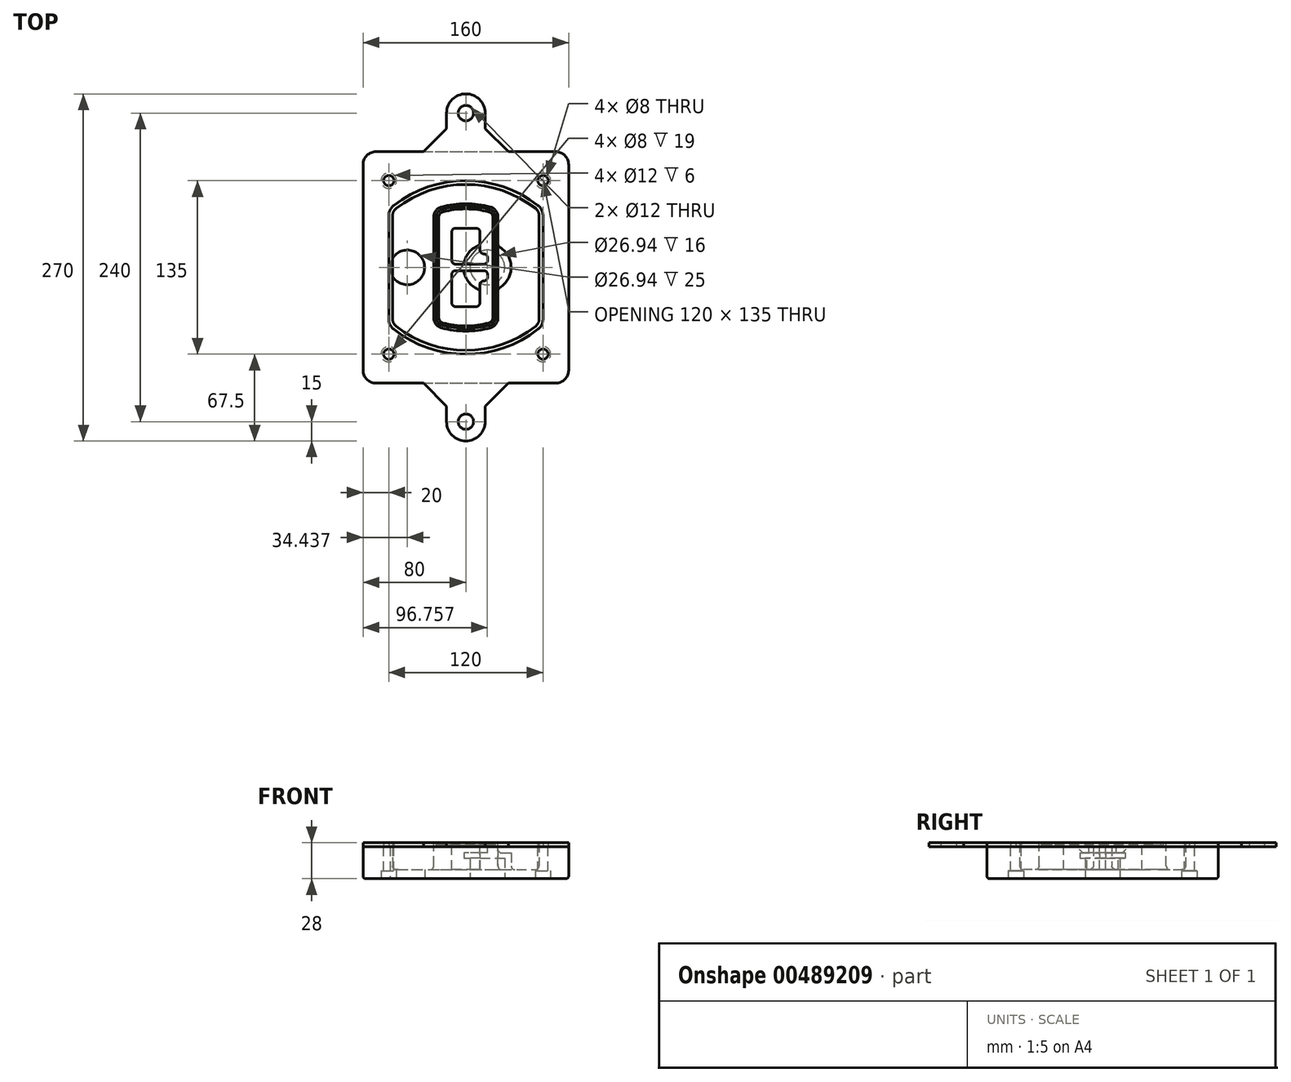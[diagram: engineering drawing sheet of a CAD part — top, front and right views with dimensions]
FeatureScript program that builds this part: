
annotation { "Feature Type Name" : "Feature", "Feature Type Description" : "" }
export const myFeature = defineFeature(function(context is Context, id is Id, definition is map)
    precondition{}
    {
        {
            var Q0;
            Q0=qCreatedBy(makeId("Top.planeOp"),FACE);
            var sketch = newSketch(context, id + "F0", { "sketchPlane" : qUnion([Q0])});
            skPoint(sketch, "E0.rect.middle", {"position": v(0, 0) * mm});
            skLineSegment(sketch, "E1.bottom", {"start": v(-70, -90) * mm, "end": v(70, -90) * mm});
            skLineSegment(sketch, "E1.top", {"start": v(-70, 90) * mm, "end": v(70, 90) * mm});
            skLineSegment(sketch, "E1.left", {"start": v(-80, -80) * mm, "end": v(-80, 80) * mm});
            skLineSegment(sketch, "E1.right", {"start": v(80, -80) * mm, "end": v(80, 80) * mm});
            skLineSegment(sketch, "E2", {"start": v(-80, 90) * mm, "end": v(80, -90) * mm, "construction": true});
            skLineSegment(sketch, "E3", {"start": v(80, 90) * mm, "end": v(-80, -90) * mm, "construction": true});
            skCircle(sketch, "E4", {"center": v(-60, 67.5) * mm, "radius": 4 * mm});
            skCircle(sketch, "E5", {"center": v(60, 67.5) * mm, "radius": 4 * mm});
            skCircle(sketch, "E6", {"center": v(60, -67.5) * mm, "radius": 4 * mm});
            skCircle(sketch, "E7", {"center": v(-60, -67.5) * mm, "radius": 4 * mm});
            skLineSegment(sketch, "E8", {"start": v(-60, 67.5) * mm, "end": v(60, 67.5) * mm, "construction": true});
            skLineSegment(sketch, "E9", {"start": v(60, 67.5) * mm, "end": v(60, -67.5) * mm, "construction": true});
            skLineSegment(sketch, "E10", {"start": v(60, -67.5) * mm, "end": v(-60, -67.5) * mm, "construction": true});
            skLineSegment(sketch, "E11", {"start": v(-60, -67.5) * mm, "end": v(-60, 67.5) * mm, "construction": true});
            skLineSegment(sketch, "E12", {"start": v(-60, 40.3) * mm, "end": v(-60, -40.3) * mm});
            skLineSegment(sketch, "E13", {"start": v(60, 40.3) * mm, "end": v(60, -40.3) * mm});
            skArc(sketch, "E14", {"start": v(56.15, 48.18) * mm, "mid": v(0, 67.5) * mm, "end": v(-56.15, 48.18) * mm});
            skArc(sketch, "E15", {"start": v(-56.15, -48.18) * mm, "mid": v(0, -67.5) * mm, "end": v(56.15, -48.18) * mm});
            skLineSegment(sketch, "E16", {"start": v(-60, 0) * mm, "end": v(60, 0) * mm, "construction": true});
            skPoint(sketch, "E17.visualSharp", {"position": v(-60, -45) * mm});
            skArc(sketch, "E17.filletArc", {"start": v(-60, -40.3) * mm, "mid": v(-58.99, -44.68) * mm, "end": v(-56.15, -48.18) * mm});
            skPoint(sketch, "E18.visualSharp", {"position": v(-60, 45) * mm});
            skArc(sketch, "E18.filletArc", {"start": v(-56.15, 48.18) * mm, "mid": v(-58.99, 44.68) * mm, "end": v(-60, 40.3) * mm});
            skPoint(sketch, "E19.visualSharp", {"position": v(60, 45) * mm});
            skArc(sketch, "E19.filletArc", {"start": v(60, 40.3) * mm, "mid": v(58.99, 44.68) * mm, "end": v(56.15, 48.18) * mm});
            skPoint(sketch, "E20.visualSharp", {"position": v(60, -45) * mm});
            skArc(sketch, "E20.filletArc", {"start": v(56.15, -48.18) * mm, "mid": v(58.99, -44.68) * mm, "end": v(60, -40.3) * mm});
            skPoint(sketch, "E21.visualSharp", {"position": v(-80, 90) * mm});
            skArc(sketch, "E21.filletArc", {"start": v(-70, 90) * mm, "mid": v(-77.07, 87.07) * mm, "end": v(-80, 80) * mm});
            skPoint(sketch, "E22.visualSharp", {"position": v(80, 90) * mm});
            skArc(sketch, "E22.filletArc", {"start": v(80, 80) * mm, "mid": v(77.07, 87.07) * mm, "end": v(70, 90) * mm});
            skPoint(sketch, "E23.visualSharp", {"position": v(80, -90) * mm});
            skArc(sketch, "E23.filletArc", {"start": v(70, -90) * mm, "mid": v(77.07, -87.07) * mm, "end": v(80, -80) * mm});
            skPoint(sketch, "E24.visualSharp", {"position": v(-80, -90) * mm});
            skArc(sketch, "E24.filletArc", {"start": v(-80, -80) * mm, "mid": v(-77.07, -87.07) * mm, "end": v(-70, -90) * mm});
            skArc(sketch, "E25.0", {"start": v(57, 40.3) * mm, "mid": v(56.3, 43.36) * mm, "end": v(54.3, 45.81) * mm});
            skLineSegment(sketch, "E25.1", {"start": v(57, 40.3) * mm, "end": v(57, -40.3) * mm});
            skArc(sketch, "E25.2", {"start": v(54.3, -45.81) * mm, "mid": v(56.3, -43.36) * mm, "end": v(57, -40.3) * mm});
            skArc(sketch, "E25.3", {"start": v(-54.3, -45.81) * mm, "mid": v(0, -64.5) * mm, "end": v(54.3, -45.81) * mm});
            skArc(sketch, "E25.4", {"start": v(-57, -40.3) * mm, "mid": v(-56.3, -43.36) * mm, "end": v(-54.3, -45.81) * mm});
            skArc(sketch, "E25.5", {"start": v(54.3, 45.81) * mm, "mid": v(0, 64.5) * mm, "end": v(-54.3, 45.81) * mm});
            skLineSegment(sketch, "E25.6", {"start": v(-57, 40.3) * mm, "end": v(-57, -40.3) * mm});
            skArc(sketch, "E25.7", {"start": v(-54.3, 45.81) * mm, "mid": v(-56.3, 43.36) * mm, "end": v(-57, 40.3) * mm});
            skArc(sketch, "E26.0", {"start": v(-58.62, 51.33) * mm, "mid": v(-62.58, 46.43) * mm, "end": v(-64, 40.3) * mm});
            skArc(sketch, "E26.1", {"start": v(58.62, 51.33) * mm, "mid": v(0, 71.5) * mm, "end": v(-58.62, 51.33) * mm});
            skArc(sketch, "E26.2", {"start": v(64, 40.3) * mm, "mid": v(62.58, 46.43) * mm, "end": v(58.62, 51.33) * mm});
            skLineSegment(sketch, "E26.3", {"start": v(64, 40.3) * mm, "end": v(64, -40.3) * mm});
            skArc(sketch, "E26.4", {"start": v(58.62, -51.33) * mm, "mid": v(62.58, -46.43) * mm, "end": v(64, -40.3) * mm});
            skLineSegment(sketch, "E26.5", {"start": v(-64, 40.3) * mm, "end": v(-64, -40.3) * mm});
            skArc(sketch, "E26.6", {"start": v(-58.62, -51.33) * mm, "mid": v(0, -71.5) * mm, "end": v(58.62, -51.33) * mm});
            skArc(sketch, "E26.7", {"start": v(-64, -40.3) * mm, "mid": v(-62.58, -46.43) * mm, "end": v(-58.62, -51.33) * mm});
            skSolve(sketch);
        }
        {
            var Q0;
            Q0=makeQuery(id+"F0.imprint","IMPRINT",FACE,{"disambiguationData":[TD([[makeQuery(id+"F0.imprint","IMPRINT",EDGE,{"derivedFrom":sQuery(id+"F0.wireOp",EDGE,"E1.bottom")}),1.0]])]});
            var Q1;
            Q1=makeQuery(id+"F0.imprint","IMPRINT",FACE,{"disambiguationData":[TD([[makeQuery(id+"F0.imprint","IMPRINT",EDGE,{"derivedFrom":sQuery(id+"F0.wireOp",EDGE,"E12")}),1.0]])]});
            var Q2;
            Q2=makeQuery(id+"F0.imprint","IMPRINT",FACE,{"disambiguationData":[TD([[makeQuery(id+"F0.imprint","IMPRINT",EDGE,{"derivedFrom":sQuery(id+"F0.wireOp",EDGE,"E25.0")}),1.0]])]});
            var Q3;
            Q3=makeQuery(id+"F0.imprint","IMPRINT",FACE,{"disambiguationData":[TD([[makeQuery(id+"F0.imprint","IMPRINT",EDGE,{"derivedFrom":sQuery(id+"F0.wireOp",EDGE,"E12")}),-1.0]])]});
            extrude(context, id + "F1", {"entities" : qUnion([Q0, Q1, Q2, Q3]), "oppositeDirection" : true, "depth" : 25 * mm});
        }
        {
            var Q0;
            Q0=makeQuery(id+"F0.imprint","IMPRINT",FACE,{"disambiguationData":[TD([[makeQuery(id+"F0.imprint","IMPRINT",EDGE,{"derivedFrom":sQuery(id+"F0.wireOp",EDGE,"E12")}),1.0]])]});
            extrude(context, id + "F2", {"entities" : qUnion([Q0]), "operationType" : NewBodyOperationType.ADD, "depth" : 3 * mm});
        }
        {
            var Q0;
            Q0=makeQuery(id+"F0.imprint","IMPRINT",FACE,{"disambiguationData":[TD([[makeQuery(id+"F0.imprint","IMPRINT",EDGE,{"derivedFrom":sQuery(id+"F0.wireOp",EDGE,"E25.0")}),1.0]])]});
            extrude(context, id + "F3", {"entities" : qUnion([Q0]), "operationType" : NewBodyOperationType.REMOVE, "oppositeDirection" : true, "depth" : 18 * mm});
        }
        {
            var Q0;
            Q0=makeQuery(id+"F2.opExtrude","CAP_FACE",FACE,{"disambiguationData":[OSD([sQuery(id+"F0.wireOp",EDGE,"E12"),sQuery(id+"F0.wireOp",EDGE,"E13"),sQuery(id+"F0.wireOp",EDGE,"E14"),sQuery(id+"F0.wireOp",EDGE,"E15"),sQuery(id+"F0.wireOp",EDGE,"E17.filletArc"),sQuery(id+"F0.wireOp",EDGE,"E18.filletArc"),sQuery(id+"F0.wireOp",EDGE,"E19.filletArc"),sQuery(id+"F0.wireOp",EDGE,"E20.filletArc"),sQuery(id+"F0.wireOp",EDGE,"E25.0"),sQuery(id+"F0.wireOp",EDGE,"E25.1"),sQuery(id+"F0.wireOp",EDGE,"E25.2"),sQuery(id+"F0.wireOp",EDGE,"E25.3"),sQuery(id+"F0.wireOp",EDGE,"E25.4"),sQuery(id+"F0.wireOp",EDGE,"E25.5"),sQuery(id+"F0.wireOp",EDGE,"E25.6"),sQuery(id+"F0.wireOp",EDGE,"E25.7")])],"isStart":false});
            var sketch = newSketch(context, id + "F4", { "sketchPlane" : qUnion([Q0])});
            skArc(sketch, "E27.0", {"start": v(-19.08, -46.97) * mm, "mid": v(0, -49.5) * mm, "end": v(19.08, -46.97) * mm});
            skArc(sketch, "E28.0", {"start": v(19.08, 46.97) * mm, "mid": v(0, 49.5) * mm, "end": v(-19.08, 46.97) * mm});
            skLineSegment(sketch, "E29", {"start": v(-25, 39.25) * mm, "end": v(-25, -39.25) * mm});
            skLineSegment(sketch, "E30", {"start": v(25, 39.25) * mm, "end": v(25, -39.25) * mm});
            skLineSegment(sketch, "E31", {"start": v(-25, 45.1) * mm, "end": v(25, 45.1) * mm, "construction": true});
            skLineSegment(sketch, "E32", {"start": v(-25, -45.1) * mm, "end": v(25, -45.1) * mm, "construction": true});
            skPoint(sketch, "E33.visualSharp", {"position": v(-25, 45.1) * mm});
            skArc(sketch, "E33.filletArc", {"start": v(-19.08, 46.97) * mm, "mid": v(-23.35, 44.11) * mm, "end": v(-25, 39.25) * mm});
            skPoint(sketch, "E34.visualSharp", {"position": v(25, 45.1) * mm});
            skArc(sketch, "E34.filletArc", {"start": v(25, 39.25) * mm, "mid": v(23.35, 44.11) * mm, "end": v(19.08, 46.97) * mm});
            skPoint(sketch, "E35.visualSharp", {"position": v(25, -45.1) * mm});
            skArc(sketch, "E35.filletArc", {"start": v(19.08, -46.97) * mm, "mid": v(23.35, -44.11) * mm, "end": v(25, -39.25) * mm});
            skPoint(sketch, "E36.visualSharp", {"position": v(-25, -45.1) * mm});
            skArc(sketch, "E36.filletArc", {"start": v(-25, -39.25) * mm, "mid": v(-23.35, -44.11) * mm, "end": v(-19.08, -46.97) * mm});
            skArc(sketch, "E37.0", {"start": v(54.3, 45.81) * mm, "mid": v(0, 64.5) * mm, "end": v(-54.3, 45.81) * mm});
            skArc(sketch, "E37.1", {"start": v(-54.3, 45.81) * mm, "mid": v(-56.3, 43.36) * mm, "end": v(-57, 40.3) * mm});
            skLineSegment(sketch, "E37.2", {"start": v(-57, 40.3) * mm, "end": v(-57, -40.3) * mm});
            skArc(sketch, "E37.3", {"start": v(-57, -40.3) * mm, "mid": v(-56.3, -43.36) * mm, "end": v(-54.3, -45.81) * mm});
            skArc(sketch, "E37.4", {"start": v(-54.3, -45.81) * mm, "mid": v(0, -64.5) * mm, "end": v(54.3, -45.81) * mm});
            skArc(sketch, "E37.5", {"start": v(54.3, -45.81) * mm, "mid": v(56.3, -43.36) * mm, "end": v(57, -40.3) * mm});
            skLineSegment(sketch, "E37.6", {"start": v(57, 40.3) * mm, "end": v(57, -40.3) * mm});
            skArc(sketch, "E37.7", {"start": v(57, 40.3) * mm, "mid": v(56.3, 43.36) * mm, "end": v(54.3, 45.81) * mm});
            skLineSegment(sketch, "E38.0", {"start": v(23, 39.25) * mm, "end": v(23, -39.25) * mm});
            skArc(sketch, "E38.1", {"start": v(18.56, -45.04) * mm, "mid": v(21.76, -42.9) * mm, "end": v(23, -39.25) * mm});
            skArc(sketch, "E38.2", {"start": v(-18.56, -45.04) * mm, "mid": v(0, -47.5) * mm, "end": v(18.56, -45.04) * mm});
            skArc(sketch, "E38.3", {"start": v(-23, -39.25) * mm, "mid": v(-21.76, -42.9) * mm, "end": v(-18.56, -45.04) * mm});
            skLineSegment(sketch, "E38.4", {"start": v(-23, 39.25) * mm, "end": v(-23, -39.25) * mm});
            skArc(sketch, "E38.5", {"start": v(23, 39.25) * mm, "mid": v(21.76, 42.9) * mm, "end": v(18.56, 45.04) * mm});
            skArc(sketch, "E38.6", {"start": v(-18.56, 45.04) * mm, "mid": v(-21.76, 42.9) * mm, "end": v(-23, 39.25) * mm});
            skArc(sketch, "E38.7", {"start": v(18.56, 45.04) * mm, "mid": v(0, 47.5) * mm, "end": v(-18.56, 45.04) * mm});
            skArc(sketch, "E39.0", {"start": v(21, 39.25) * mm, "mid": v(20.18, 41.68) * mm, "end": v(18.04, 43.1) * mm});
            skLineSegment(sketch, "E39.1", {"start": v(21, 39.25) * mm, "end": v(21, -39.25) * mm});
            skArc(sketch, "E39.2", {"start": v(18.04, -43.1) * mm, "mid": v(20.18, -41.68) * mm, "end": v(21, -39.25) * mm});
            skArc(sketch, "E39.3", {"start": v(-18.04, -43.1) * mm, "mid": v(0, -45.5) * mm, "end": v(18.04, -43.1) * mm});
            skArc(sketch, "E39.4", {"start": v(-21, -39.25) * mm, "mid": v(-20.18, -41.68) * mm, "end": v(-18.04, -43.1) * mm});
            skArc(sketch, "E39.5", {"start": v(18.04, 43.1) * mm, "mid": v(0, 45.5) * mm, "end": v(-18.04, 43.1) * mm});
            skLineSegment(sketch, "E39.6", {"start": v(-21, 39.25) * mm, "end": v(-21, -39.25) * mm});
            skArc(sketch, "E39.7", {"start": v(-18.04, 43.1) * mm, "mid": v(-20.18, 41.68) * mm, "end": v(-21, 39.25) * mm});
            skLineSegment(sketch, "E40", {"start": v(-25, 0) * mm, "end": v(25, 0) * mm, "construction": true});
            skLineSegment(sketch, "E41", {"start": v(-11, 5.5) * mm, "end": v(-11, 27.5) * mm});
            skLineSegment(sketch, "E42", {"start": v(-8, 30.5) * mm, "end": v(8, 30.5) * mm});
            skLineSegment(sketch, "E43", {"start": v(11, 27.5) * mm, "end": v(11, 13.5) * mm});
            skLineSegment(sketch, "E44", {"start": v(14, 10.5) * mm, "end": v(14, 10.5) * mm});
            skLineSegment(sketch, "E45", {"start": v(17, 7.5) * mm, "end": v(17, 5.5) * mm});
            skLineSegment(sketch, "E46", {"start": v(14, 2.5) * mm, "end": v(-8, 2.5) * mm});
            skPoint(sketch, "E47.visualSharp", {"position": v(-11, 30.5) * mm});
            skArc(sketch, "E47.filletArc", {"start": v(-8, 30.5) * mm, "mid": v(-10.12, 29.62) * mm, "end": v(-11, 27.5) * mm});
            skPoint(sketch, "E48.visualSharp", {"position": v(11, 30.5) * mm});
            skArc(sketch, "E48.filletArc", {"start": v(11, 27.5) * mm, "mid": v(10.12, 29.62) * mm, "end": v(8, 30.5) * mm});
            skPoint(sketch, "E49.visualSharp", {"position": v(11, 10.5) * mm});
            skArc(sketch, "E49.filletArc", {"start": v(11, 13.5) * mm, "mid": v(11.88, 11.38) * mm, "end": v(14, 10.5) * mm});
            skPoint(sketch, "E50.visualSharp", {"position": v(17, 10.5) * mm});
            skArc(sketch, "E50.filletArc", {"start": v(17, 7.5) * mm, "mid": v(16.12, 9.62) * mm, "end": v(14, 10.5) * mm});
            skPoint(sketch, "E51.visualSharp", {"position": v(17, 2.5) * mm});
            skArc(sketch, "E51.filletArc", {"start": v(14, 2.5) * mm, "mid": v(16.12, 3.38) * mm, "end": v(17, 5.5) * mm});
            skPoint(sketch, "E52.visualSharp", {"position": v(-11, 2.5) * mm});
            skArc(sketch, "E52.filletArc", {"start": v(-11, 5.5) * mm, "mid": v(-10.12, 3.38) * mm, "end": v(-8, 2.5) * mm});
            skLineSegment(sketch, "E53.0.MirrorCS", {"start": v(14, -2.5) * mm, "end": v(-8, -2.5) * mm});
            skArc(sketch, "E54.0.MirrorCS", {"start": v(-11, -5.5) * mm, "mid": v(-10.12, -3.38) * mm, "end": v(-8, -2.5) * mm});
            skLineSegment(sketch, "E55.0.MirrorCS", {"start": v(-11, -5.5) * mm, "end": v(-11, -27.5) * mm});
            skArc(sketch, "E56.0.MirrorCS", {"start": v(-8, -30.5) * mm, "mid": v(-10.12, -29.62) * mm, "end": v(-11, -27.5) * mm});
            skLineSegment(sketch, "E57.0.MirrorCS", {"start": v(-8, -30.5) * mm, "end": v(8, -30.5) * mm});
            skArc(sketch, "E58.0.MirrorCS", {"start": v(11, -27.5) * mm, "mid": v(10.12, -29.62) * mm, "end": v(8, -30.5) * mm});
            skLineSegment(sketch, "E59.0.MirrorCS", {"start": v(11, -27.5) * mm, "end": v(11, -13.5) * mm});
            skArc(sketch, "E60.0.MirrorCS", {"start": v(11, -13.5) * mm, "mid": v(11.88, -11.38) * mm, "end": v(14, -10.5) * mm});
            skArc(sketch, "E61.0.MirrorCS", {"start": v(17, -7.5) * mm, "mid": v(16.12, -9.62) * mm, "end": v(14, -10.5) * mm});
            skLineSegment(sketch, "E62.0.MirrorCS", {"start": v(17, -7.5) * mm, "end": v(17, -5.5) * mm});
            skArc(sketch, "E63.0.MirrorCS", {"start": v(14, -2.5) * mm, "mid": v(16.12, -3.38) * mm, "end": v(17, -5.5) * mm});
            skSolve(sketch);
        }
        {
            var Q0;
            Q0=makeQuery(id+"F4.imprint","IMPRINT",FACE,{"disambiguationData":[TD([[makeQuery(id+"F4.imprint","IMPRINT",EDGE,{"derivedFrom":sQuery(id+"F4.wireOp",EDGE,"E27.0")}),1.0]])]});
            var Q1;
            Q1=makeQuery(id+"F4.imprint","IMPRINT",FACE,{"disambiguationData":[TD([[makeQuery(id+"F4.imprint","IMPRINT",EDGE,{"derivedFrom":sQuery(id+"F4.wireOp",EDGE,"E38.0")}),-1.0]])]});
            var Q2;
            Q2=makeQuery(id+"F4.imprint","IMPRINT",FACE,{"disambiguationData":[TD([[makeQuery(id+"F4.imprint","IMPRINT",EDGE,{"derivedFrom":sQuery(id+"F4.wireOp",EDGE,"E39.0")}),1.0]])]});
            extrude(context, id + "F5", {"entities" : qUnion([Q0, Q1, Q2]), "operationType" : NewBodyOperationType.ADD, "endBound" : BoundingType.UP_TO_NEXT, "oppositeDirection" : true, "depth" : 25 * mm});
        }
        {
            var Q0;
            Q0=makeQuery(id+"F4.imprint","IMPRINT",FACE,{"disambiguationData":[TD([[makeQuery(id+"F4.imprint","IMPRINT",EDGE,{"derivedFrom":sQuery(id+"F4.wireOp",EDGE,"E38.0")}),-1.0]])]});
            extrude(context, id + "F6", {"entities" : qUnion([Q0]), "operationType" : NewBodyOperationType.REMOVE, "oppositeDirection" : true, "depth" : 2 * mm});
        }
        {
            var Q0;
            Q0=makeQuery(id+"F1.opExtrude","CAP_FACE",FACE,{"disambiguationData":[OSD([sQuery(id+"F0.wireOp",EDGE,"E1.bottom"),sQuery(id+"F0.wireOp",EDGE,"E1.top"),sQuery(id+"F0.wireOp",EDGE,"E1.left"),sQuery(id+"F0.wireOp",EDGE,"E1.right"),sQuery(id+"F0.wireOp",EDGE,"E4"),sQuery(id+"F0.wireOp",EDGE,"E5"),sQuery(id+"F0.wireOp",EDGE,"E6"),sQuery(id+"F0.wireOp",EDGE,"E7"),sQuery(id+"F0.wireOp",EDGE,"E21.filletArc"),sQuery(id+"F0.wireOp",EDGE,"E22.filletArc"),sQuery(id+"F0.wireOp",EDGE,"E23.filletArc"),sQuery(id+"F0.wireOp",EDGE,"E24.filletArc")])],"isStart":false});
            var sketch = newSketch(context, id + "F7", { "sketchPlane" : qUnion([Q0])});
            skCircle(sketch, "E64", {"center": v(16.76, 0) * mm, "radius": 13.47 * mm});
            skCircle(sketch, "E65", {"center": v(-45.56, 0) * mm, "radius": 13.47 * mm});
            skLineSegment(sketch, "E66", {"start": v(80, 0) * mm, "end": v(-80, 0) * mm});
            skCircle(sketch, "E67", {"center": v(16.76, 0) * mm, "radius": 18.47 * mm});
            skCircle(sketch, "E68", {"center": v(60, -67.5) * mm, "radius": 6 * mm});
            skCircle(sketch, "E69", {"center": v(-60, -67.5) * mm, "radius": 6 * mm});
            skCircle(sketch, "E70", {"center": v(-60, 67.5) * mm, "radius": 6 * mm});
            skCircle(sketch, "E71", {"center": v(60, 67.5) * mm, "radius": 6 * mm});
            skSolve(sketch);
        }
        {
            var Q0;
            {var subQ1=sQuery(id+"F7.wireOp",EDGE,"E66");var subQ4=sQuery(id+"F7.wireOp",EDGE,"E64");var subQ6=makeQuery(id+"F7.imprint","INTERSECT",VERTEX,{"disambiguationData":[OD(0.0)],"derivedFrom":[subQ4,subQ1]});Q0=makeQuery(id+"F7.imprint","IMPRINT",FACE,{"disambiguationData":[TD([[makeQuery(id+"F7.imprint","IMPRINT",EDGE,{"disambiguationData":[TD([[subQ6,-1.0]])],"derivedFrom":subQ4}),-1.0]])]});}
            var Q1;
            {var subQ0=sQuery(id+"F7.wireOp",EDGE,"E66");var subQ1=sQuery(id+"F7.wireOp",EDGE,"E64");var subQ3=makeQuery(id+"F7.imprint","INTERSECT",VERTEX,{"disambiguationData":[OD(0.0)],"derivedFrom":[subQ1,subQ0]});Q1=makeQuery(id+"F7.imprint","IMPRINT",FACE,{"disambiguationData":[TD([[makeQuery(id+"F7.imprint","IMPRINT",EDGE,{"disambiguationData":[TD([[subQ3,-1.0]])],"derivedFrom":subQ1}),1.0]])]});}
            var Q2;
            {var subQ0=sQuery(id+"F7.wireOp",EDGE,"E66");var subQ1=sQuery(id+"F7.wireOp",EDGE,"E64");var subQ3=makeQuery(id+"F7.imprint","INTERSECT",VERTEX,{"disambiguationData":[OD(0.0)],"derivedFrom":[subQ1,subQ0]});Q2=makeQuery(id+"F7.imprint","IMPRINT",FACE,{"disambiguationData":[TD([[makeQuery(id+"F7.imprint","IMPRINT",EDGE,{"disambiguationData":[TD([[subQ3,1.0]])],"derivedFrom":subQ1}),1.0]])]});}
            var Q3;
            {var subQ1=sQuery(id+"F7.wireOp",EDGE,"E66");var subQ4=sQuery(id+"F7.wireOp",EDGE,"E64");var subQ6=makeQuery(id+"F7.imprint","INTERSECT",VERTEX,{"disambiguationData":[OD(0.0)],"derivedFrom":[subQ4,subQ1]});Q3=makeQuery(id+"F7.imprint","IMPRINT",FACE,{"disambiguationData":[TD([[makeQuery(id+"F7.imprint","IMPRINT",EDGE,{"disambiguationData":[TD([[subQ6,1.0]])],"derivedFrom":subQ4}),-1.0]])]});}
            extrude(context, id + "F8", {"entities" : qUnion([Q0, Q1, Q2, Q3]), "operationType" : NewBodyOperationType.ADD, "oppositeDirection" : true, "depth" : 20 * mm});
        }
        {
            var Q0;
            {var subQ0=sQuery(id+"F7.wireOp",EDGE,"E66");var subQ1=sQuery(id+"F7.wireOp",EDGE,"E64");var subQ3=makeQuery(id+"F7.imprint","INTERSECT",VERTEX,{"disambiguationData":[OD(0.0)],"derivedFrom":[subQ1,subQ0]});Q0=makeQuery(id+"F7.imprint","IMPRINT",FACE,{"disambiguationData":[TD([[makeQuery(id+"F7.imprint","IMPRINT",EDGE,{"disambiguationData":[TD([[subQ3,-1.0]])],"derivedFrom":subQ1}),1.0]])]});}
            var Q1;
            {var subQ0=sQuery(id+"F7.wireOp",EDGE,"E66");var subQ1=sQuery(id+"F7.wireOp",EDGE,"E64");var subQ3=makeQuery(id+"F7.imprint","INTERSECT",VERTEX,{"disambiguationData":[OD(0.0)],"derivedFrom":[subQ1,subQ0]});Q1=makeQuery(id+"F7.imprint","IMPRINT",FACE,{"disambiguationData":[TD([[makeQuery(id+"F7.imprint","IMPRINT",EDGE,{"disambiguationData":[TD([[subQ3,1.0]])],"derivedFrom":subQ1}),1.0]])]});}
            extrude(context, id + "F9", {"entities" : qUnion([Q0, Q1]), "operationType" : NewBodyOperationType.REMOVE, "oppositeDirection" : true, "depth" : 16 * mm});
        }
        {
            var Q0;
            {var subQ0=sQuery(id+"F7.wireOp",EDGE,"E66");var subQ1=sQuery(id+"F7.wireOp",EDGE,"E65");var subQ3=makeQuery(id+"F7.imprint","INTERSECT",VERTEX,{"disambiguationData":[OD(0.0)],"derivedFrom":[subQ1,subQ0]});Q0=makeQuery(id+"F7.imprint","IMPRINT",FACE,{"disambiguationData":[TD([[makeQuery(id+"F7.imprint","IMPRINT",EDGE,{"disambiguationData":[TD([[subQ3,-1.0]])],"derivedFrom":subQ1}),1.0]])]});}
            var Q1;
            {var subQ0=sQuery(id+"F7.wireOp",EDGE,"E66");var subQ1=sQuery(id+"F7.wireOp",EDGE,"E65");var subQ3=makeQuery(id+"F7.imprint","INTERSECT",VERTEX,{"disambiguationData":[OD(0.0)],"derivedFrom":[subQ1,subQ0]});Q1=makeQuery(id+"F7.imprint","IMPRINT",FACE,{"disambiguationData":[TD([[makeQuery(id+"F7.imprint","IMPRINT",EDGE,{"disambiguationData":[TD([[subQ3,1.0]])],"derivedFrom":subQ1}),1.0]])]});}
            extrude(context, id + "F10", {"entities" : qUnion([Q0, Q1]), "operationType" : NewBodyOperationType.REMOVE, "oppositeDirection" : true, "depth" : 25 * mm});
        }
        {
            var Q0;
            Q0=makeQuery(id+"F7.imprint","IMPRINT",FACE,{"disambiguationData":[TD([[makeQuery(id+"F7.imprint","IMPRINT",EDGE,{"derivedFrom":sQuery(id+"F7.wireOp",EDGE,"E68")}),1.0]])]});
            var Q1;
            Q1=makeQuery(id+"F7.imprint","IMPRINT",FACE,{"disambiguationData":[TD([[makeQuery(id+"F7.imprint","IMPRINT",EDGE,{"derivedFrom":makeQuery(id+"F1.opExtrude","CAP_EDGE",EDGE,{"disambiguationData":[OSD([sQuery(id+"F0.wireOp",EDGE,"E5")])],"isStart":false})}),-1.0]])]});
            var Q2;
            Q2=makeQuery(id+"F7.imprint","IMPRINT",FACE,{"disambiguationData":[TD([[makeQuery(id+"F7.imprint","IMPRINT",EDGE,{"derivedFrom":sQuery(id+"F7.wireOp",EDGE,"E69")}),1.0]])]});
            var Q3;
            Q3=makeQuery(id+"F7.imprint","IMPRINT",FACE,{"disambiguationData":[TD([[makeQuery(id+"F7.imprint","IMPRINT",EDGE,{"derivedFrom":makeQuery(id+"F1.opExtrude","CAP_EDGE",EDGE,{"disambiguationData":[OSD([sQuery(id+"F0.wireOp",EDGE,"E4")])],"isStart":false})}),-1.0]])]});
            var Q4;
            Q4=makeQuery(id+"F7.imprint","IMPRINT",FACE,{"disambiguationData":[TD([[makeQuery(id+"F7.imprint","IMPRINT",EDGE,{"derivedFrom":sQuery(id+"F7.wireOp",EDGE,"E70")}),1.0]])]});
            var Q5;
            Q5=makeQuery(id+"F7.imprint","IMPRINT",FACE,{"disambiguationData":[TD([[makeQuery(id+"F7.imprint","IMPRINT",EDGE,{"derivedFrom":makeQuery(id+"F1.opExtrude","CAP_EDGE",EDGE,{"disambiguationData":[OSD([sQuery(id+"F0.wireOp",EDGE,"E7")])],"isStart":false})}),-1.0]])]});
            var Q6;
            Q6=makeQuery(id+"F7.imprint","IMPRINT",FACE,{"disambiguationData":[TD([[makeQuery(id+"F7.imprint","IMPRINT",EDGE,{"derivedFrom":sQuery(id+"F7.wireOp",EDGE,"E71")}),1.0]])]});
            var Q7;
            Q7=makeQuery(id+"F7.imprint","IMPRINT",FACE,{"disambiguationData":[TD([[makeQuery(id+"F7.imprint","IMPRINT",EDGE,{"derivedFrom":makeQuery(id+"F1.opExtrude","CAP_EDGE",EDGE,{"disambiguationData":[OSD([sQuery(id+"F0.wireOp",EDGE,"E6")])],"isStart":false})}),-1.0]])]});
            extrude(context, id + "F11", {"entities" : qUnion([Q0, Q1, Q2, Q3, Q4, Q5, Q6, Q7]), "operationType" : NewBodyOperationType.REMOVE, "oppositeDirection" : true, "depth" : 6 * mm});
        }
        {
            var Q0;
            Q0=makeQuery(id+"F9.boolean.opBoolean","COPY",FACE,{"derivedFrom":makeQuery(id+"F9.opExtrude","CAP_FACE",FACE,{"disambiguationData":[OSD([sQuery(id+"F7.wireOp",EDGE,"E64")])],"isStart":false})});
            var sketch = newSketch(context, id + "F12", { "sketchPlane" : qUnion([Q0])});
            skArc(sketch, "E72.0", {"start": v(11, 17.55) * mm, "mid": v(2.57, 11.82) * mm, "end": v(-1.54, 2.5) * mm});
            skArc(sketch, "E72.1", {"start": v(-1.54, -2.5) * mm, "mid": v(2.57, -11.82) * mm, "end": v(11, -17.55) * mm});
            skLineSegment(sketch, "E73", {"start": v(-1.54, -2.5) * mm, "end": v(14, -2.5) * mm});
            skLineSegment(sketch, "E74.0", {"start": v(14, 2.5) * mm, "end": v(-1.54, 2.5) * mm});
            skArc(sketch, "E74.1", {"start": v(14, 2.5) * mm, "mid": v(16.12, 3.38) * mm, "end": v(17, 5.5) * mm});
            skLineSegment(sketch, "E74.2", {"start": v(17, 7.5) * mm, "end": v(17, 5.5) * mm});
            skArc(sketch, "E74.3", {"start": v(17, 7.5) * mm, "mid": v(16.12, 9.62) * mm, "end": v(14, 10.5) * mm});
            skArc(sketch, "E74.4", {"start": v(11, 13.5) * mm, "mid": v(11.88, 11.38) * mm, "end": v(14, 10.5) * mm});
            skLineSegment(sketch, "E74.5", {"start": v(11, 17.55) * mm, "end": v(11, 13.5) * mm});
            skLineSegment(sketch, "E74.7", {"start": v(14, -2.5) * mm, "end": v(-1.54, -2.5) * mm});
            skArc(sketch, "E74.8", {"start": v(14, -2.5) * mm, "mid": v(16.12, -3.38) * mm, "end": v(17, -5.5) * mm});
            skLineSegment(sketch, "E74.9", {"start": v(17, -7.5) * mm, "end": v(17, -5.5) * mm});
            skArc(sketch, "E74.10", {"start": v(17, -7.5) * mm, "mid": v(16.12, -9.62) * mm, "end": v(14, -10.5) * mm});
            skArc(sketch, "E74.11", {"start": v(11, -13.5) * mm, "mid": v(11.88, -11.38) * mm, "end": v(14, -10.5) * mm});
            skLineSegment(sketch, "E74.12", {"start": v(11, -17.55) * mm, "end": v(11, -13.5) * mm});
            skPoint(sketch, "E75.orphan", {"position": v(11, -27.5) * mm});
            skPoint(sketch, "E76.orphan", {"position": v(-8, -2.5) * mm});
            skPoint(sketch, "E77.orphan", {"position": v(-8, 2.5) * mm});
            skPoint(sketch, "E78.orphan", {"position": v(11, 27.5) * mm});
            skSolve(sketch);
        }
        {
            var Q0;
            {var subQ7=sQuery(id+"F12.wireOp",EDGE,"E72.0");var subQ14=sQuery(id+"F12.wireOp",EDGE,"E72.1");var subQ16=sQuery(id+"F12.wireOp",EDGE,"E74.1");var subQ18=sQuery(id+"F12.wireOp",EDGE,"E74.8");Q0=qUnion([makeQuery(id+"F12.imprint","IMPRINT",FACE,{"disambiguationData":[TD([[makeQuery(id+"F12.imprint","IMPRINT",EDGE,{"derivedFrom":subQ7}),1.0]])]}),makeQuery(id+"F12.imprint","IMPRINT",FACE,{"disambiguationData":[TD([[makeQuery(id+"F12.imprint","IMPRINT",EDGE,{"derivedFrom":subQ14}),1.0]])]}),makeQuery(id+"F12.imprint","IMPRINT",FACE,{"disambiguationData":[TD([[makeQuery(id+"F12.imprint","IMPRINT",EDGE,{"derivedFrom":subQ16}),1.0]])]}),makeQuery(id+"F12.imprint","IMPRINT",FACE,{"disambiguationData":[TD([[makeQuery(id+"F12.imprint","IMPRINT",EDGE,{"derivedFrom":subQ18}),-1.0]])]})]);}
            var Q1;
            Q1=makeQuery(id+"F5.boolean.opBoolean","SPLIT",FACE,{"disambiguationData":[TD([makeQuery(id+"F5.opExtrude","SWEPT_FACE",FACE,{"disambiguationData":[OSD([sQuery(id+"F4.wireOp",EDGE,"E41")])]})])],"derivedFrom":makeQuery(id+"F3.boolean.opBoolean","COPY",FACE,{"derivedFrom":makeQuery(id+"F3.opExtrude","CAP_FACE",FACE,{"disambiguationData":[OSD([sQuery(id+"F0.wireOp",EDGE,"E25.0"),sQuery(id+"F0.wireOp",EDGE,"E25.1"),sQuery(id+"F0.wireOp",EDGE,"E25.2"),sQuery(id+"F0.wireOp",EDGE,"E25.3"),sQuery(id+"F0.wireOp",EDGE,"E25.4"),sQuery(id+"F0.wireOp",EDGE,"E25.5"),sQuery(id+"F0.wireOp",EDGE,"E25.6"),sQuery(id+"F0.wireOp",EDGE,"E25.7")])],"isStart":false})})});
            extrude(context, id + "F13", {"entities" : qUnion([Q0]), "operationType" : NewBodyOperationType.REMOVE, "endBound" : BoundingType.UP_TO_SURFACE, "endBoundEntityFace" : qUnion([Q1]), "depth" : 25 * mm});
        }
        {
            var Q0;
            Q0=makeQuery(id+"F3.boolean.opBoolean","COPY",EDGE,{"derivedFrom":makeQuery(id+"F3.opExtrude","CAP_EDGE",EDGE,{"disambiguationData":[OSD([sQuery(id+"F0.wireOp",EDGE,"E25.6")])],"isStart":false})});
            var Q1;
            Q1=makeQuery(id+"F8.boolean.opBoolean","INTERSECT",EDGE,{"derivedFrom":[makeQuery(id+"F5.opExtrude","SWEPT_FACE",FACE,{"disambiguationData":[OSD([sQuery(id+"F4.wireOp",EDGE,"E30")])]}),makeQuery(id+"F8.opExtrude","CAP_FACE",FACE,{"disambiguationData":[OSD([sQuery(id+"F7.wireOp",EDGE,"E67")])],"isStart":false})]});
            var Q2;
            Q2=makeQuery(id+"F8.boolean.opBoolean","INTERSECT",EDGE,{"disambiguationData":[OD(1.0)],"derivedFrom":[makeQuery(id+"F5.opExtrude","SWEPT_FACE",FACE,{"disambiguationData":[OSD([sQuery(id+"F4.wireOp",EDGE,"E30")])]}),makeQuery(id+"F8.opExtrude","SWEPT_FACE",FACE,{"disambiguationData":[OSD([sQuery(id+"F7.wireOp",EDGE,"E67")])]})]});
            var Q3;
            {var subQ0=sQuery(id+"F4.wireOp",EDGE,"E30");Q3=makeQuery(id+"F8.boolean.opBoolean","SPLIT",EDGE,{"disambiguationData":[TD([makeQuery(id+"F5.opExtrude","SWEPT_FACE",FACE,{"disambiguationData":[OSD([sQuery(id+"F4.wireOp",EDGE,"E35.filletArc")])]})])],"derivedFrom":makeQuery(id+"F5.opExtrude","CAP_EDGE",EDGE,{"disambiguationData":[OSD([subQ0])],"isStart":false})});}
            var Q4;
            {var subQ0=sQuery(id+"F0.wireOp",EDGE,"E25.7");var subQ1=sQuery(id+"F0.wireOp",EDGE,"E25.1");var subQ2=sQuery(id+"F0.wireOp",EDGE,"E25.6");var subQ3=sQuery(id+"F0.wireOp",EDGE,"E25.5");var subQ4=sQuery(id+"F0.wireOp",EDGE,"E25.4");var subQ5=sQuery(id+"F0.wireOp",EDGE,"E25.0");var subQ6=sQuery(id+"F0.wireOp",EDGE,"E25.2");var subQ7=sQuery(id+"F0.wireOp",EDGE,"E25.3");Q4=makeQuery(id+"F8.boolean.opBoolean","INTERSECT",EDGE,{"derivedFrom":[makeQuery(id+"F5.boolean.opBoolean","SPLIT",FACE,{"disambiguationData":[TD([makeQuery(id+"F2.opExtrude","SWEPT_FACE",FACE,{"disambiguationData":[OSD([subQ5])]})])],"derivedFrom":makeQuery(id+"F3.boolean.opBoolean","COPY",FACE,{"derivedFrom":makeQuery(id+"F3.opExtrude","CAP_FACE",FACE,{"disambiguationData":[OSD([subQ5,subQ1,subQ6,subQ7,subQ4,subQ3,subQ2,subQ0])],"isStart":false})})}),makeQuery(id+"F8.opExtrude","SWEPT_FACE",FACE,{"disambiguationData":[OSD([sQuery(id+"F7.wireOp",EDGE,"E67")])]})]});}
            var Q5;
            Q5=makeQuery(id+"F8.boolean.opBoolean","INTERSECT",EDGE,{"disambiguationData":[OD(0.0)],"derivedFrom":[makeQuery(id+"F5.opExtrude","SWEPT_FACE",FACE,{"disambiguationData":[OSD([sQuery(id+"F4.wireOp",EDGE,"E30")])]}),makeQuery(id+"F8.opExtrude","SWEPT_FACE",FACE,{"disambiguationData":[OSD([sQuery(id+"F7.wireOp",EDGE,"E67")])]})]});
            fillet(context, id + "F14", {"entities" : qUnion([Q0, Q1, Q2, Q3, Q4, Q5]), "radius" : 3 * mm, "tangentPropagation" : true, "allowEdgeOverflow" : false});
        }
        {
            var Q0;
            Q0=makeQuery(id+"F1.opExtrude","CAP_EDGE",EDGE,{"disambiguationData":[OSD([sQuery(id+"F0.wireOp",EDGE,"E1.bottom")])],"isStart":false});
            fillet(context, id + "F15", {"entities" : qUnion([Q0]), "radius" : 2 * mm, "tangentPropagation" : true, "allowEdgeOverflow" : false});
        }
        {
            var Q0;
            {var subQ0=sQuery(id+"F0.wireOp",EDGE,"E21.filletArc");var subQ1=sQuery(id+"F0.wireOp",EDGE,"E7");var subQ2=sQuery(id+"F0.wireOp",EDGE,"E6");var subQ3=sQuery(id+"F0.wireOp",EDGE,"E5");var subQ4=sQuery(id+"F0.wireOp",EDGE,"E4");var subQ5=sQuery(id+"F0.wireOp",EDGE,"E22.filletArc");var subQ6=sQuery(id+"F0.wireOp",EDGE,"E1.bottom");var subQ7=sQuery(id+"F0.wireOp",EDGE,"E1.right");var subQ8=sQuery(id+"F0.wireOp",EDGE,"E1.top");var subQ9=sQuery(id+"F0.wireOp",EDGE,"E1.left");var subQ10=sQuery(id+"F0.wireOp",EDGE,"E23.filletArc");var subQ11=sQuery(id+"F0.wireOp",EDGE,"E24.filletArc");Q0=makeQuery(id+"F2.boolean.opBoolean","SPLIT",FACE,{"disambiguationData":[TD([makeQuery(id+"F1.opExtrude","SWEPT_FACE",FACE,{"disambiguationData":[OSD([subQ6])]})])],"derivedFrom":makeQuery(id+"F1.opExtrude","CAP_FACE",FACE,{"disambiguationData":[OSD([subQ6,subQ8,subQ9,subQ7,subQ4,subQ3,subQ2,subQ1,subQ0,subQ5,subQ10,subQ11])],"isStart":true})});}
            var sketch = newSketch(context, id + "F16", { "sketchPlane" : qUnion([Q0])});
            skPoint(sketch, "E79.1", {"position": v(77.07, 87.07) * mm});
            skArc(sketch, "E80.0", {"start": v(-70, 90) * mm, "mid": v(-77.07, 87.07) * mm, "end": v(-80, 80) * mm});
            skLineSegment(sketch, "E81.0", {"start": v(-80, -80) * mm, "end": v(-80, 80) * mm});
            skPoint(sketch, "E82.0", {"position": v(-77.07, -87.07) * mm});
            skLineSegment(sketch, "E83.0", {"start": v(-70, -90) * mm, "end": v(70, -90) * mm});
            skArc(sketch, "E84.0", {"start": v(-80, -80) * mm, "mid": v(-77.07, -87.07) * mm, "end": v(-70, -90) * mm});
            skArc(sketch, "E85.0", {"start": v(70, -90) * mm, "mid": v(77.07, -87.07) * mm, "end": v(80, -80) * mm});
            skLineSegment(sketch, "E86.0", {"start": v(80, -80) * mm, "end": v(80, 80) * mm});
            skCircle(sketch, "E87.0", {"center": v(60, 67.5) * mm, "radius": 4 * mm});
            skCircle(sketch, "E88.0", {"center": v(-60, 67.5) * mm, "radius": 4 * mm});
            skCircle(sketch, "E89.0", {"center": v(-60, -67.5) * mm, "radius": 4 * mm});
            skCircle(sketch, "E90.0", {"center": v(60, -67.5) * mm, "radius": 4 * mm});
            skLineSegment(sketch, "E91.0", {"start": v(-70, 90) * mm, "end": v(70, 90) * mm});
            skArc(sketch, "E92.0", {"start": v(80, 80) * mm, "mid": v(77.07, 87.07) * mm, "end": v(70, 90) * mm});
            skArc(sketch, "E93.0", {"start": v(56.15, 48.18) * mm, "mid": v(0, 67.5) * mm, "end": v(-56.15, 48.18) * mm});
            skArc(sketch, "E93.1", {"start": v(-56.15, 48.18) * mm, "mid": v(-58.99, 44.68) * mm, "end": v(-60, 40.3) * mm});
            skLineSegment(sketch, "E93.2", {"start": v(-60, 40.3) * mm, "end": v(-60, -40.3) * mm});
            skArc(sketch, "E93.3", {"start": v(-60, -40.3) * mm, "mid": v(-58.99, -44.68) * mm, "end": v(-56.15, -48.18) * mm});
            skArc(sketch, "E93.4", {"start": v(-56.15, -48.18) * mm, "mid": v(0, -67.5) * mm, "end": v(56.15, -48.18) * mm});
            skArc(sketch, "E93.5", {"start": v(56.15, -48.18) * mm, "mid": v(58.99, -44.68) * mm, "end": v(60, -40.3) * mm});
            skLineSegment(sketch, "E93.6", {"start": v(60, 40.3) * mm, "end": v(60, -40.3) * mm});
            skArc(sketch, "E93.7", {"start": v(60, 40.3) * mm, "mid": v(58.99, 44.68) * mm, "end": v(56.15, 48.18) * mm});
            skLineSegment(sketch, "E94", {"start": v(0, 90) * mm, "end": v(0, 120) * mm, "construction": true});
            skLineSegment(sketch, "E95", {"start": v(-33, 90) * mm, "end": v(-15, 108) * mm});
            skLineSegment(sketch, "E96", {"start": v(-15, 108) * mm, "end": v(-15, 120) * mm});
            skLineSegment(sketch, "E97", {"start": v(33, 90) * mm, "end": v(15, 108) * mm});
            skLineSegment(sketch, "E98", {"start": v(15, 108) * mm, "end": v(15, 120) * mm});
            skArc(sketch, "E99", {"start": v(15, 120) * mm, "mid": v(0, 135) * mm, "end": v(-15, 120) * mm});
            skCircle(sketch, "E100", {"center": v(0, 120) * mm, "radius": 6 * mm});
            skLineSegment(sketch, "E101", {"start": v(-80, 0) * mm, "end": v(80, 0) * mm, "construction": true});
            skLineSegment(sketch, "E102.MirrorCS", {"start": v(15, -108) * mm, "end": v(15, -120) * mm});
            skLineSegment(sketch, "E103.MirrorCS", {"start": v(-15, -108) * mm, "end": v(-15, -120) * mm});
            skLineSegment(sketch, "E104.MirrorCS", {"start": v(0, -90) * mm, "end": v(0, -120) * mm, "construction": true});
            skCircle(sketch, "E105.MirrorC", {"center": v(0, -120) * mm, "radius": 6 * mm});
            skLineSegment(sketch, "E106.MirrorCS", {"start": v(-33, -90) * mm, "end": v(-15, -108) * mm});
            skArc(sketch, "E107.MirrorCS", {"start": v(15, -120) * mm, "mid": v(0, -135) * mm, "end": v(-15, -120) * mm});
            skLineSegment(sketch, "E108.MirrorCS", {"start": v(33, -90) * mm, "end": v(15, -108) * mm});
            skSolve(sketch);
        }
        {
            var Q0;
            {var subQ1=sQuery(id+"F16.wireOp",EDGE,"E95");Q0=makeQuery(id+"F16.imprint","IMPRINT",FACE,{"disambiguationData":[TD([[makeQuery(id+"F16.imprint","IMPRINT",EDGE,{"derivedFrom":subQ1}),-1.0]])]});}
            var Q1;
            {var subQ4=sQuery(id+"F16.wireOp",EDGE,"E80.0");Q1=makeQuery(id+"F16.imprint","IMPRINT",FACE,{"disambiguationData":[TD([[makeQuery(id+"F16.imprint","IMPRINT",EDGE,{"derivedFrom":subQ4}),1.0]])]});}
            var Q2;
            Q2=makeQuery(id+"F16.imprint","IMPRINT",FACE,{"disambiguationData":[TD([[makeQuery(id+"F16.imprint","IMPRINT",EDGE,{"derivedFrom":sQuery(id+"F16.wireOp",EDGE,"E102.MirrorCS")}),-1.0]])]});
            var Q3;
            Q3=makeQuery(id+"F2.opExtrude","CAP_FACE",FACE,{"disambiguationData":[OSD([sQuery(id+"F0.wireOp",EDGE,"E12"),sQuery(id+"F0.wireOp",EDGE,"E13"),sQuery(id+"F0.wireOp",EDGE,"E14"),sQuery(id+"F0.wireOp",EDGE,"E15"),sQuery(id+"F0.wireOp",EDGE,"E17.filletArc"),sQuery(id+"F0.wireOp",EDGE,"E18.filletArc"),sQuery(id+"F0.wireOp",EDGE,"E19.filletArc"),sQuery(id+"F0.wireOp",EDGE,"E20.filletArc"),sQuery(id+"F0.wireOp",EDGE,"E25.0"),sQuery(id+"F0.wireOp",EDGE,"E25.1"),sQuery(id+"F0.wireOp",EDGE,"E25.2"),sQuery(id+"F0.wireOp",EDGE,"E25.3"),sQuery(id+"F0.wireOp",EDGE,"E25.4"),sQuery(id+"F0.wireOp",EDGE,"E25.5"),sQuery(id+"F0.wireOp",EDGE,"E25.6"),sQuery(id+"F0.wireOp",EDGE,"E25.7")])],"isStart":false});
            extrude(context, id + "F17", {"entities" : qUnion([Q0, Q1, Q2]), "endBound" : BoundingType.UP_TO_SURFACE, "endBoundEntityFace" : qUnion([Q3]), "depth" : 25 * mm});
        }
    });
